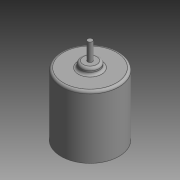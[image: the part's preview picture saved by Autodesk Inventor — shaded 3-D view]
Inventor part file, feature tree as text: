
AUTODESK INVENTOR PART (.ipt)
format: ipt  version: 2018 (Build 220112000, 112)  size: 126,464 bytes
history: native  units: mm
features: extrude x3, sketch x3, fillet x2, other x1
ambient origin geometry x8: Origin, YZ Plane, XZ Plane, XY Plane, X Axis, Y Axis, Z Axis, Center Point
bodies: Body1 (feature_tree)
feature tree (9):
  other  "ソリッド1"
  extrude  "押し出し1"  Depth=36.0mm
  extrude  "押し出し2"  Depth=39.0mm TaperAngle=0.0deg
  extrude  "押し出し3"  Depth=11.5mm
  fillet  "フィレット1"  Radius=3.8mm
  fillet  "フィレット2"  Radius=3.0mm
  sketch  "スケッチ1"
  sketch  "スケッチ2"
  sketch  "スケッチ3"
